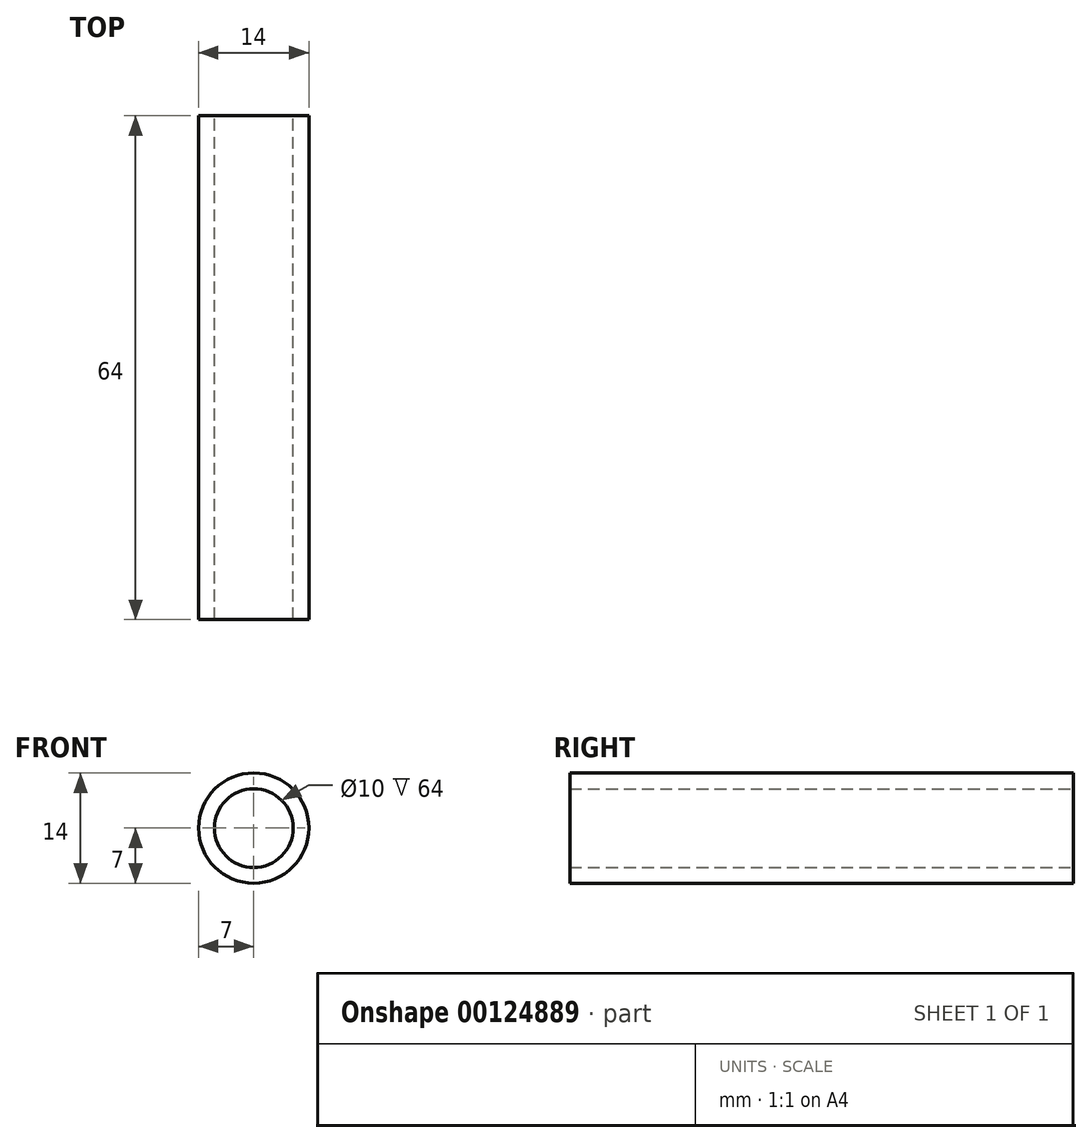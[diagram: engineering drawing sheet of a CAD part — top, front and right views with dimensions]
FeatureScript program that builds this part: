
annotation { "Feature Type Name" : "Feature", "Feature Type Description" : "" }
export const myFeature = defineFeature(function(context is Context, id is Id, definition is map)
    precondition{}
    {
        {
            var Q0;
            Q0=qCreatedBy(makeId("Front.planeOp"),FACE);
            var sketch = newSketch(context, id + "F0", { "sketchPlane" : qUnion([Q0])});
            skCircle(sketch, "E0", {"center": v(0, 0) * mm, "radius": 7 * mm});
            skCircle(sketch, "E1.0", {"center": v(0, 0) * mm, "radius": 5 * mm});
            skSolve(sketch);
        }
        {
            var Q0;
            Q0=makeQuery(id+"F0.imprint","IMPRINT",FACE,{"disambiguationData":[TD([[makeQuery(id+"F0.imprint","IMPRINT",EDGE,{"derivedFrom":sQuery(id+"F0.wireOp",EDGE,"E0")}),1.0]])]});
            extrude(context, id + "F1", {"entities" : qUnion([Q0]), "endBound" : BoundingType.SYMMETRIC, "depth" : 64 * mm});
        }
    });
